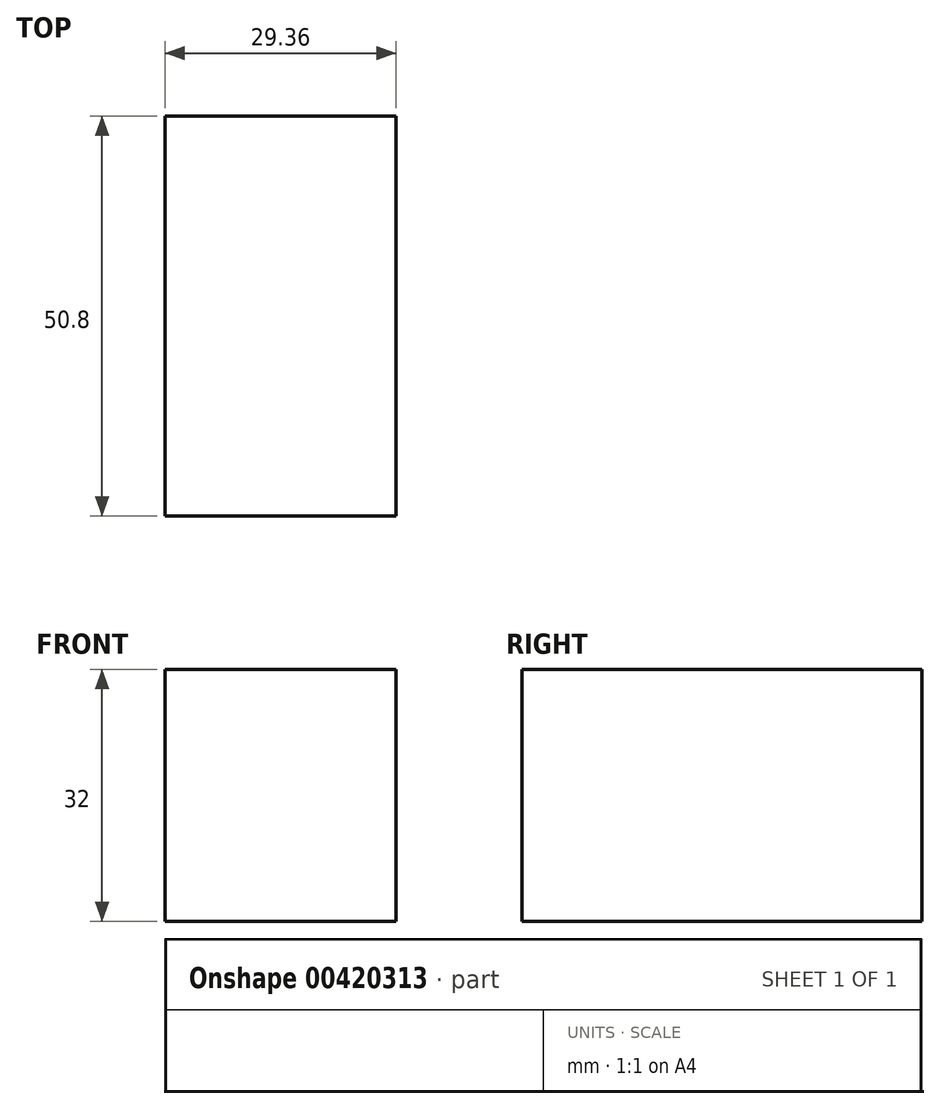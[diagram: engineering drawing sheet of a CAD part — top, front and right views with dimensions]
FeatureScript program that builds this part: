
annotation { "Feature Type Name" : "Feature", "Feature Type Description" : "" }
export const myFeature = defineFeature(function(context is Context, id is Id, definition is map)
    precondition{}
    {
        {
            var Q0;
            Q0=qCreatedBy(makeId("Front.planeOp"),FACE);
            var sketch = newSketch(context, id + "F0", { "sketchPlane" : qUnion([Q0])});
            skLineSegment(sketch, "E0.bottom", {"start": v(-44.07, 32) * mm, "end": v(-14.71, 32) * mm});
            skLineSegment(sketch, "E0.top", {"start": v(-44.07, 0) * mm, "end": v(-14.71, 0) * mm});
            skLineSegment(sketch, "E0.left", {"start": v(-44.07, 32) * mm, "end": v(-44.07, 0) * mm});
            skLineSegment(sketch, "E0.right", {"start": v(-14.71, 32) * mm, "end": v(-14.71, 0) * mm});
            skSolve(sketch);
        }
        {
            var Q0;
            Q0 = qSketchRegion(id + "F0", true);
            extrude(context, id + "F1", {"entities" : qUnion([Q0]), "depth" : 25.4 * mm});
        }
        {
            var Q0;
            Q0=makeQuery(id+"F1.opExtrude","CAP_FACE",FACE,{"disambiguationData":[OSD([sQuery(id+"F0.wireOp",EDGE,"E0.bottom"),sQuery(id+"F0.wireOp",EDGE,"E0.top"),sQuery(id+"F0.wireOp",EDGE,"E0.left"),sQuery(id+"F0.wireOp",EDGE,"E0.right")])],"isStart":false});
            var sketch = newSketch(context, id + "F2", { "sketchPlane" : qUnion([Q0])});
            skLineSegment(sketch, "E1", {"start": v(-29.4, -18.18) * mm, "end": v(-29.4, 9.81) * mm});
            skPoint(sketch, "E1.startSnap0", {"position": v(-29.4, 0) * mm});
            skLineSegment(sketch, "E2", {"start": v(-29.4, 9.81) * mm, "end": v(-29.4, -36.35) * mm});
            skSolve(sketch);
        }
        {
            var Q0;
            Q0=makeQuery(id+"F2.imprint","IMPRINT",FACE,{"disambiguationData":[TD([[makeQuery(id+"F2.imprint","IMPRINT",EDGE,{"derivedFrom":makeQuery(id+"F1.opExtrude","CAP_EDGE",EDGE,{"disambiguationData":[OSD([sQuery(id+"F0.wireOp",EDGE,"E0.bottom")])],"isStart":false})}),-1.0]])]});
            extrude(context, id + "F3", {"entities" : qUnion([Q0]), "operationType" : NewBodyOperationType.ADD, "depth" : 25.4 * mm});
        }
    });
